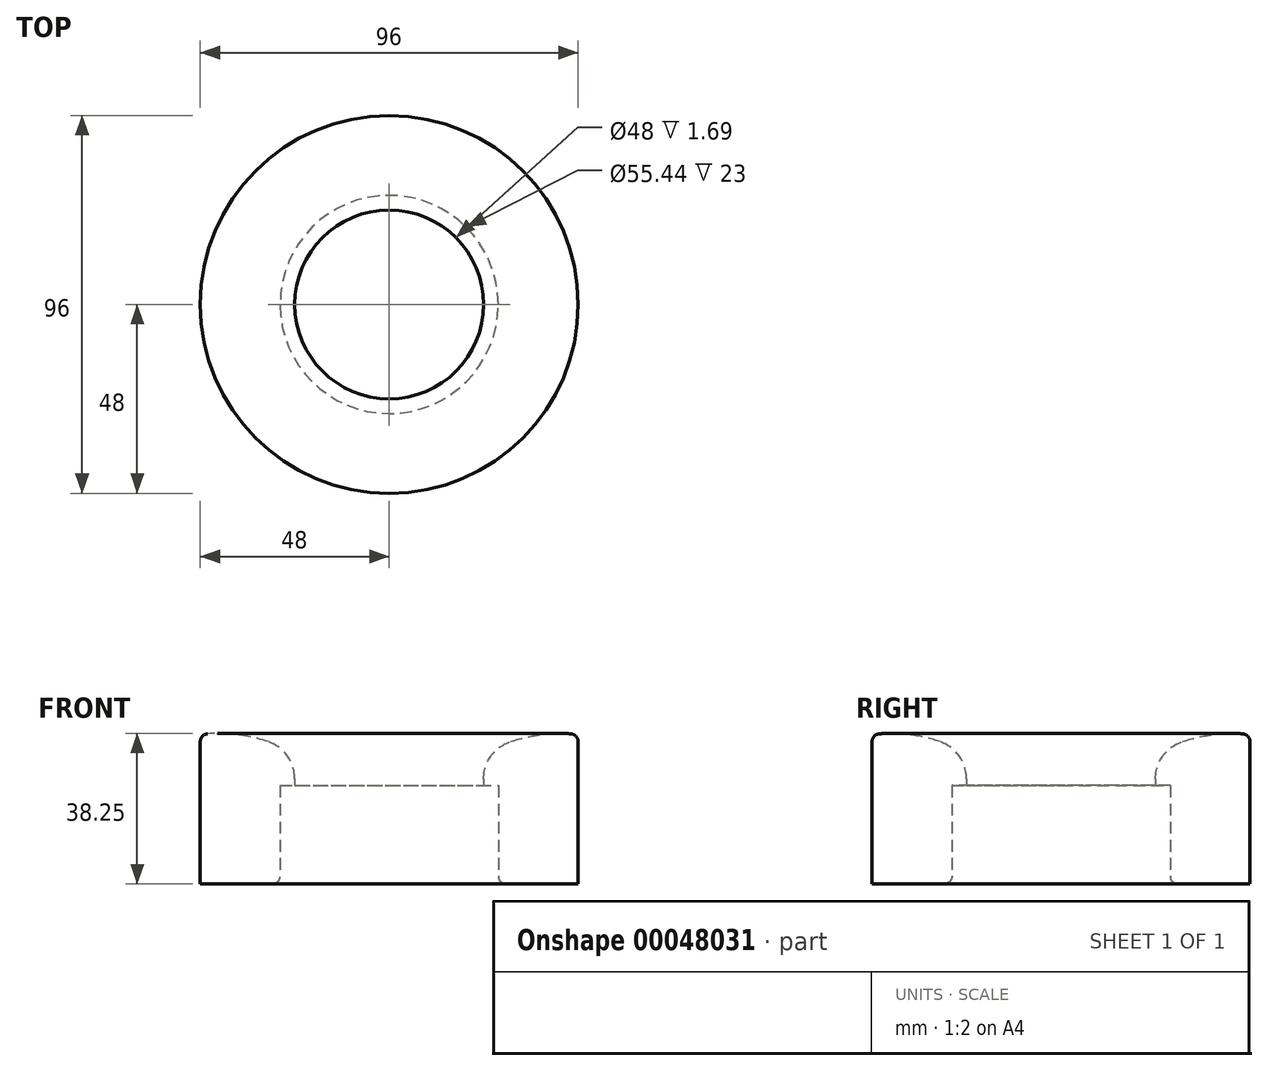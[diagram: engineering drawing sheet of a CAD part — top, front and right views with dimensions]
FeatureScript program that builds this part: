
annotation { "Feature Type Name" : "Feature", "Feature Type Description" : "" }
export const myFeature = defineFeature(function(context is Context, id is Id, definition is map)
    precondition{}
    {
        {
            var Q0;
            Q0=qCreatedBy(makeId("Right.planeOp"),FACE);
            var sketch = newSketch(context, id + "F0", { "sketchPlane" : qUnion([Q0])});
            skLineSegment(sketch, "E0", {"start": v(27.72, 0) * mm, "end": v(27.72, 25) * mm});
            skLineSegment(sketch, "E1", {"start": v(48, 0) * mm, "end": v(48, 38) * mm});
            skLineSegment(sketch, "E2", {"start": v(0, 0) * mm, "end": v(0, 40.45) * mm, "construction": true});
            skLineSegment(sketch, "E3", {"start": v(27.72, 25) * mm, "end": v(24, 25) * mm});
            skLineSegment(sketch, "E4", {"start": v(24, 25) * mm, "end": v(24, 26.69) * mm});
            skArc(sketch, "E5", {"start": v(48, 38) * mm, "mid": v(39.31, 38.02) * mm, "end": v(30.82, 36.17) * mm});
            skPoint(sketch, "E6.visualSharp", {"position": v(24, 33.15) * mm});
            skArc(sketch, "E6.filletArc", {"start": v(30.82, 36.17) * mm, "mid": v(25.88, 32.53) * mm, "end": v(24, 26.69) * mm});
            skLineSegment(sketch, "E7", {"start": v(27.72, 0) * mm, "end": v(48, 0) * mm});
            skSolve(sketch);
        }
        {
            var Q0;
            Q0 = qSketchRegion(id + "F0", true);
            var Q1;
            Q1=sQuery(id+"F0.wireOp",EDGE,"E2");
            revolve(context, id + "F1", {"entities" : qUnion([Q0]), "axis" : qUnion([Q1]), "revolveType" : RevolveType.FULL});
        }
        {
            var Q0;
            Q0=makeQuery(id+"F1.opRevolve","SWEPT_EDGE",EDGE,{"disambiguationData":[OSD([sQuery(id+"F0.wireOp",EDGE,"E1"),sQuery(id+"F0.wireOp",EDGE,"E5")])]});
            var Q1;
            Q1=makeQuery(id+"F1.opRevolve","SWEPT_EDGE",EDGE,{"disambiguationData":[OSD([sQuery(id+"F0.wireOp",EDGE,"E0"),sQuery(id+"F0.wireOp",EDGE,"E7")])]});
            fillet(context, id + "F2", {"entities" : qUnion([Q0, Q1]), "radius" : 2 * mm, "tangentPropagation" : true, "allowEdgeOverflow" : false});
        }
    });
